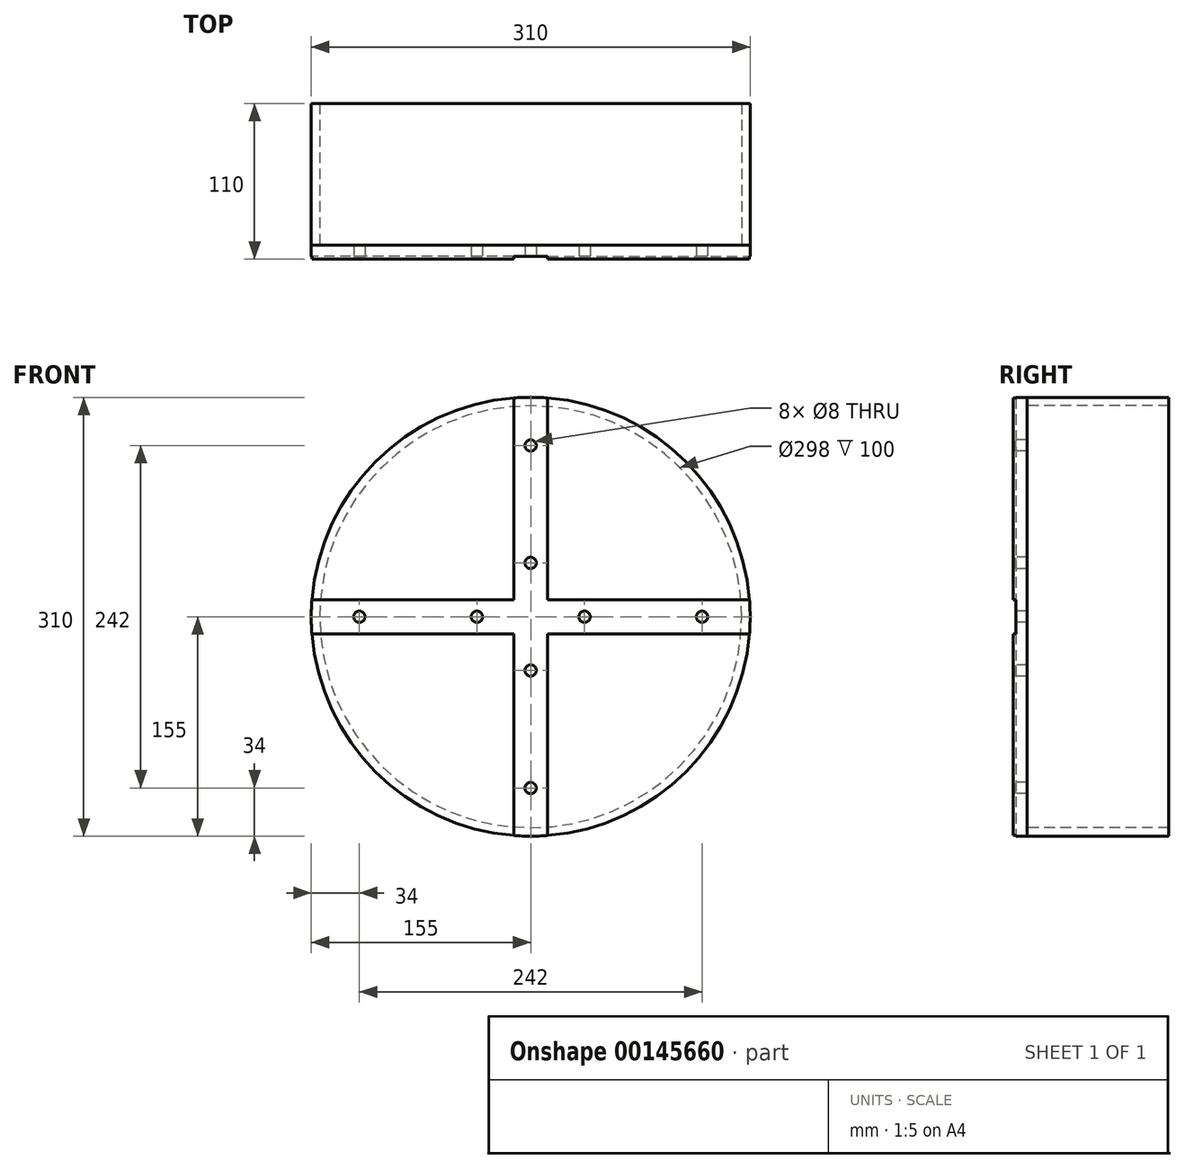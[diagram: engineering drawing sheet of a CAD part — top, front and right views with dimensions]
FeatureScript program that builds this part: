
annotation { "Feature Type Name" : "Feature", "Feature Type Description" : "" }
export const myFeature = defineFeature(function(context is Context, id is Id, definition is map)
    precondition{}
    {
        {
            var Q0;
            Q0=qCreatedBy(makeId("Front.planeOp"),FACE);
            var sketch = newSketch(context, id + "F0", { "sketchPlane" : qUnion([Q0])});
            skCircle(sketch, "E0", {"center": v(0, 0) * mm, "radius": 155 * mm});
            skSolve(sketch);
        }
        {
            var Q0;
            Q0 = qSketchRegion(id + "F0", true);
            extrude(context, id + "F1", {"entities" : qUnion([Q0]), "depth" : 10 * mm});
        }
        {
            var Q0;
            Q0=makeQuery(id+"F1.opExtrude","CAP_FACE",FACE,{"disambiguationData":[OSD([sQuery(id+"F0.wireOp",EDGE,"E0")])],"isStart":true});
            var sketch = newSketch(context, id + "F2", { "sketchPlane" : qUnion([Q0])});
            skCircle(sketch, "E1", {"center": v(0, 0) * mm, "radius": 155 * mm});
            skCircle(sketch, "E2", {"center": v(0, 0) * mm, "radius": 149 * mm});
            skSolve(sketch);
        }
        {
            var Q0;
            Q0 = qSketchRegion(id + "F2", true);
            extrude(context, id + "F3", {"entities" : qUnion([Q0]), "depth" : 100 * mm});
        }
        {
            var Q0;
            Q0=makeQuery(id+"F1.opExtrude","CAP_FACE",FACE,{"disambiguationData":[OSD([sQuery(id+"F0.wireOp",EDGE,"E0")])],"isStart":false});
            var sketch = newSketch(context, id + "F4", { "sketchPlane" : qUnion([Q0])});
            skLineSegment(sketch, "E3.0", {"start": v(-12, 12) * mm, "end": v(-155, 12) * mm});
            skLineSegment(sketch, "E3.1", {"start": v(12, 12) * mm, "end": v(155, 12) * mm});
            skLineSegment(sketch, "E4.0", {"start": v(12, -12) * mm, "end": v(155, -12) * mm});
            skLineSegment(sketch, "E4.1", {"start": v(-12, -12) * mm, "end": v(-155, -12) * mm});
            skArc(sketch, "E5", {"start": v(12, 154.53) * mm, "mid": v(0, 155) * mm, "end": v(-12, 154.53) * mm});
            skLineSegment(sketch, "E6.0", {"start": v(-12, 155) * mm, "end": v(-12, 12) * mm});
            skLineSegment(sketch, "E7.0", {"start": v(12, 155) * mm, "end": v(12, 12) * mm});
            skLineSegment(sketch, "E8.trimOffspring", {"start": v(12, -12) * mm, "end": v(12, -155) * mm});
            skLineSegment(sketch, "E9.trimOffspring", {"start": v(-12, -12) * mm, "end": v(-12, -155) * mm});
            skArc(sketch, "E10.trimOffspring", {"start": v(-154.53, 12) * mm, "mid": v(-155, 0) * mm, "end": v(-154.53, -12) * mm});
            skArc(sketch, "E11.trimOffspring", {"start": v(-12, -154.53) * mm, "mid": v(0, -155) * mm, "end": v(12, -154.53) * mm});
            skArc(sketch, "E12.trimOffspring", {"start": v(154.53, -12) * mm, "mid": v(155, 0) * mm, "end": v(154.53, 12) * mm});
            skSolve(sketch);
        }
        {
            var Q0;
            Q0 = qSketchRegion(id + "F4", true);
            extrude(context, id + "F5", {"entities" : qUnion([Q0]), "operationType" : NewBodyOperationType.REMOVE, "oppositeDirection" : true, "depth" : 2 * mm});
        }
        {
            var Q0;
            Q0=makeQuery(id+"F5.boolean.opBoolean","COPY",FACE,{"derivedFrom":makeQuery(id+"F5.opExtrude","CAP_FACE",FACE,{"disambiguationData":[OSD([sQuery(id+"F4.wireOp",EDGE,"E3.0"),sQuery(id+"F4.wireOp",EDGE,"E3.1"),sQuery(id+"F4.wireOp",EDGE,"E4.0"),sQuery(id+"F4.wireOp",EDGE,"E4.1"),sQuery(id+"F4.wireOp",EDGE,"E5"),sQuery(id+"F4.wireOp",EDGE,"E6.0"),sQuery(id+"F4.wireOp",EDGE,"E7.0"),sQuery(id+"F4.wireOp",EDGE,"E8.trimOffspring"),sQuery(id+"F4.wireOp",EDGE,"E9.trimOffspring"),sQuery(id+"F4.wireOp",EDGE,"E10.trimOffspring"),sQuery(id+"F4.wireOp",EDGE,"E11.trimOffspring"),sQuery(id+"F4.wireOp",EDGE,"E12.trimOffspring")])],"isStart":false})});
            var sketch = newSketch(context, id + "F6", { "sketchPlane" : qUnion([Q0])});
            skPoint(sketch, "E13.endSnap0", {"position": v(0, 12) * mm});
            skCircle(sketch, "E14", {"center": v(0, 121) * mm, "radius": 4 * mm});
            skCircle(sketch, "E15", {"center": v(0, 38) * mm, "radius": 4 * mm});
            skCircle(sketch, "E16.1.0", {"center": v(-121, 0) * mm, "radius": 4 * mm});
            skCircle(sketch, "E16.1.1", {"center": v(-38, 0) * mm, "radius": 4 * mm});
            skCircle(sketch, "E16.2.0", {"center": v(0, -121) * mm, "radius": 4 * mm});
            skCircle(sketch, "E16.2.1", {"center": v(0, -38) * mm, "radius": 4 * mm});
            skCircle(sketch, "E16.3.0", {"center": v(121, 0) * mm, "radius": 4 * mm});
            skCircle(sketch, "E16.3.1", {"center": v(38, 0) * mm, "radius": 4 * mm});
            skPoint(sketch, "E16.center", {"position": v(0, 0) * mm});
            skSolve(sketch);
        }
        {
            var Q0;
            Q0 = qSketchRegion(id + "F6", true);
            extrude(context, id + "F7", {"entities" : qUnion([Q0]), "operationType" : NewBodyOperationType.REMOVE, "endBound" : BoundingType.THROUGH_ALL, "oppositeDirection" : true, "depth" : 25 * mm});
        }
    });
